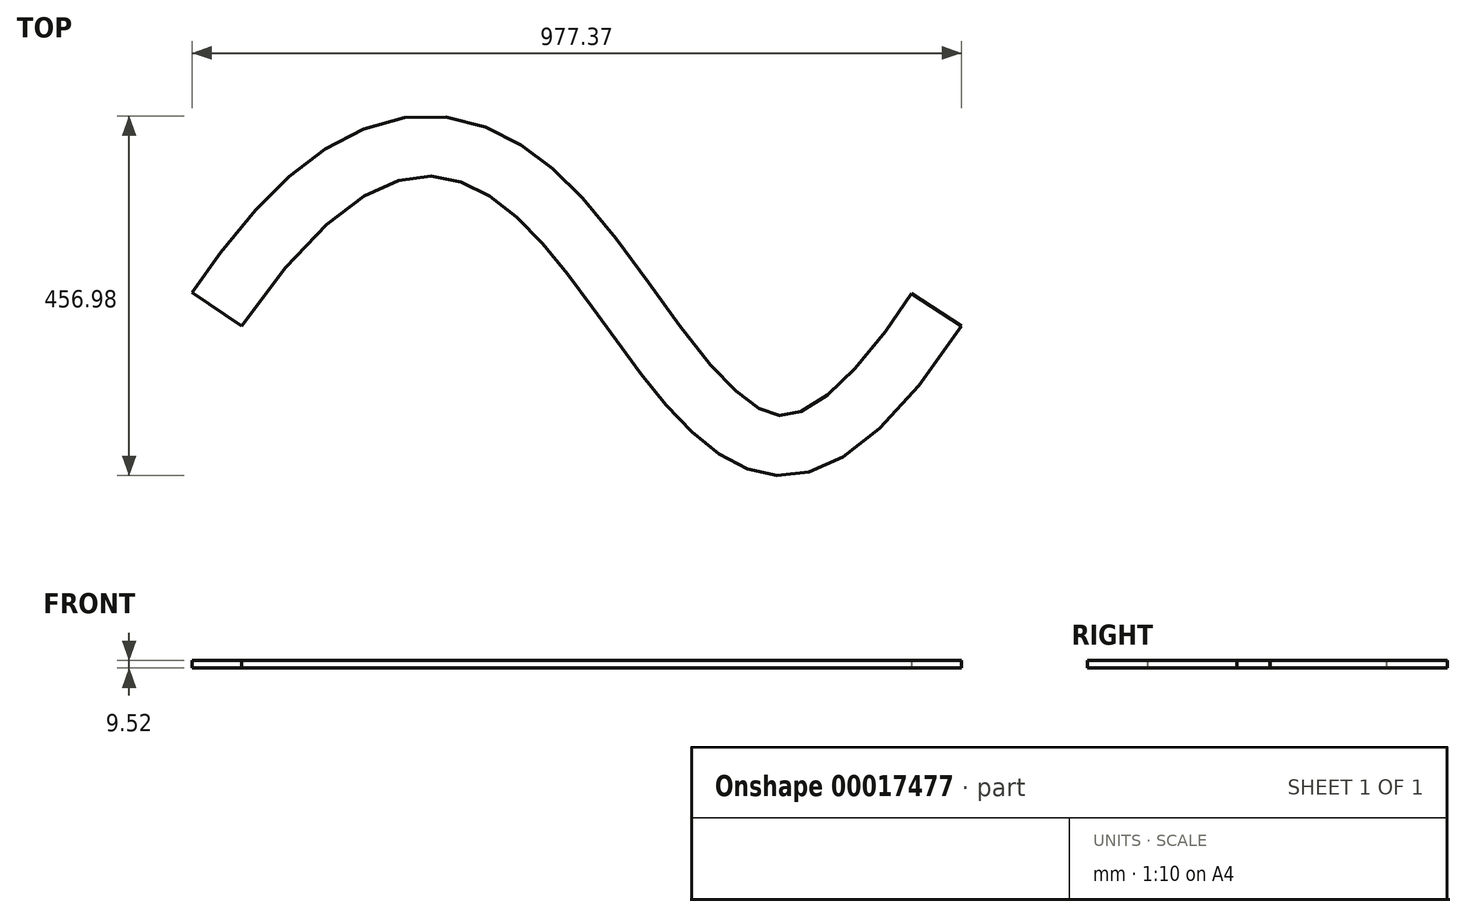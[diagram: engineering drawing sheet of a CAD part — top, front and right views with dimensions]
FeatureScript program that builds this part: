
annotation { "Feature Type Name" : "Feature", "Feature Type Description" : "" }
export const myFeature = defineFeature(function(context is Context, id is Id, definition is map)
    precondition{}
    {
        {
            var Q0;
            Q0=qCreatedBy(makeId("Top.planeOp"),FACE);
            var sketch = newSketch(context, id + "F0", { "sketchPlane" : qUnion([Q0])});
            skFitSpline(sketch, "E0", {"points": [v(451.84, 0) * mm, v(0, 0) * mm, v(-462.56, 0) * mm], "startDerivative": vector(-1290.19, -1987.87) * mm, "endDerivative": vector(-1339.1, -1964.7) * mm});
            skLineSegment(sketch, "E1", {"start": v(-238.07, 329.37) * mm, "end": v(238.07, -329.37) * mm, "construction": true});
            skFitSpline(sketch, "E2.0", {"points": [v(387.92, 41.48) * mm, v(375.33, 22.08) * mm, v(357.2, -3.9) * mm, v(334.69, -32.6) * mm, v(318.7, -51.23) * mm, v(303.66, -67.05) * mm, v(289.68, -80.18) * mm, v(276.83, -90.74) * mm, v(265.23, -98.91) * mm, v(254.97, -104.93) * mm, v(246.08, -109.07) * mm, v(238.53, -111.68) * mm, v(232.14, -113.12) * mm, v(226.6, -113.72) * mm, v(221.5, -113.67) * mm, v(216.4, -113.02) * mm, v(210.9, -111.7) * mm, v(204.8, -109.54) * mm, v(197.97, -106.35) * mm, v(190.42, -102.01) * mm, v(182.22, -96.44) * mm, v(173.46, -89.6) * mm, v(164.24, -81.55) * mm, v(154.66, -72.33) * mm, v(141.5, -58.6) * mm, v(124.46, -38.94) * mm, v(103.4, -12.21) * mm, v(81.83, 16.84) * mm, v(59.76, 47.41) * mm, v(37.08, 78.75) * mm, v(13.58, 110.16) * mm, v(-11.04, 141.02) * mm, v(-32.85, 165.74) * mm, v(-51.38, 184.6) * mm, v(-65.93, 198.2) * mm, v(-81.23, 211.14) * mm, v(-97.41, 223.28) * mm, v(-114.6, 234.47) * mm, v(-132.91, 244.49) * mm, v(-152.42, 253.06) * mm, v(-173.14, 259.88) * mm, v(-194.95, 264.6) * mm, v(-217.63, 266.91) * mm, v(-240.84, 266.6) * mm, v(-264.2, 263.58) * mm, v(-287.41, 257.89) * mm, v(-310.24, 249.67) * mm, v(-332.58, 239.07) * mm, v(-354.45, 226.22) * mm, v(-375.94, 211.2) * mm, v(-397.16, 194.05) * mm, v(-418.25, 174.74) * mm, v(-439.31, 153.22) * mm, v(-460.48, 129.41) * mm, v(-488.95, 94.5) * mm, v(-510.73, 64.62) * mm, v(-525.53, 42.92) * mm]});
            skLineSegment(sketch, "E3", {"start": v(-525.53, 42.92) * mm, "end": v(-462.56, 0) * mm});
            skLineSegment(sketch, "E4", {"start": v(387.92, 41.48) * mm, "end": v(451.84, 0) * mm});
            skSolve(sketch);
        }
        {
            var Q0;
            Q0=makeQuery(id+"F0.imprint","IMPRINT",FACE,{"disambiguationData":[TD([[makeQuery(id+"F0.imprint","IMPRINT",EDGE,{"derivedFrom":sQuery(id+"F0.wireOp",EDGE,"E0")}),-1.0]])]});
            extrude(context, id + "F1", {"entities" : qUnion([Q0]), "endBound" : BoundingType.SYMMETRIC, "depth" : 9.52 * mm});
        }
    });
